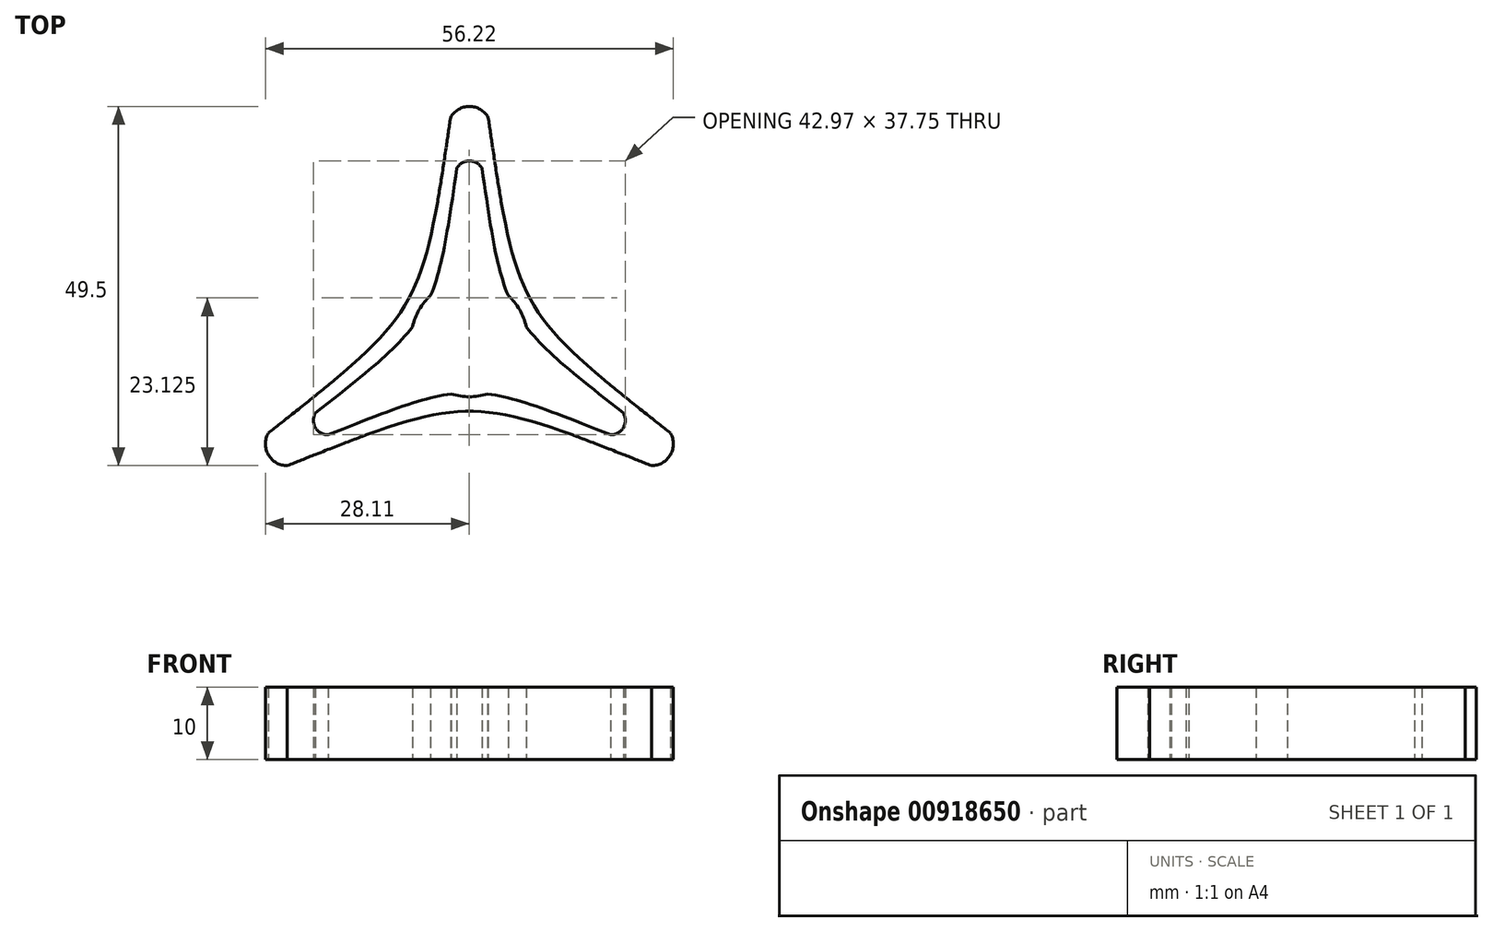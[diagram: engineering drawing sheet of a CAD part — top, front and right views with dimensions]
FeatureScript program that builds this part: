
annotation { "Feature Type Name" : "Feature", "Feature Type Description" : "" }
export const myFeature = defineFeature(function(context is Context, id is Id, definition is map)
    precondition{}
    {
        {
            var Q0;
            Q0=qCreatedBy(makeId("Top.planeOp"),FACE);
            var sketch = newSketch(context, id + "F0", { "sketchPlane" : qUnion([Q0])});
            skCircle(sketch, "E0", {"center": v(0, 0) * mm, "radius": 8 * mm});
            skCircle(sketch, "E1", {"center": v(0, 0) * mm, "radius": 35 * mm});
            skCircle(sketch, "E2", {"center": v(0, 0) * mm, "radius": 26.5 * mm});
            skCircle(sketch, "E3", {"center": v(0, 0) * mm, "radius": 5.5 * mm});
            skCircle(sketch, "E4", {"center": v(0, 0) * mm, "radius": 7.5 * mm});
            skCircle(sketch, "E5.cCircle", {"center": v(0, 0) * mm, "radius": 5.5 * mm, "construction": true});
            skLineSegment(sketch, "E5.0", {"start": v(0, -5.5) * mm, "end": v(-4.76, 2.75) * mm});
            skLineSegment(sketch, "E5.1", {"start": v(-4.76, 2.75) * mm, "end": v(4.76, 2.75) * mm});
            skLineSegment(sketch, "E5.2", {"start": v(4.76, 2.75) * mm, "end": v(0, -5.5) * mm});
            skCircle(sketch, "E6.cCircle", {"center": v(0, 0) * mm, "radius": 7.5 * mm, "construction": true});
            skLineSegment(sketch, "E6.0", {"start": v(0, -7.5) * mm, "end": v(-6.5, 3.75) * mm});
            skLineSegment(sketch, "E6.1", {"start": v(-6.5, 3.75) * mm, "end": v(6.5, 3.75) * mm});
            skLineSegment(sketch, "E6.2", {"start": v(6.5, 3.75) * mm, "end": v(0, -7.5) * mm});
            skCircle(sketch, "E7.cCircle", {"center": v(0, 0) * mm, "radius": 26.5 * mm, "construction": true});
            skPoint(sketch, "E7.cCircle.perimeterSnap0", {"position": v(0, 3.75) * mm});
            skLineSegment(sketch, "E7.0", {"start": v(1.73, 23.5) * mm, "end": v(21.22, -10.25) * mm});
            skPoint(sketch, "E7.0.startSnap0", {"position": v(0, 3.75) * mm});
            skLineSegment(sketch, "E7.1", {"start": v(19.49, -13.25) * mm, "end": v(-19.49, -13.25) * mm});
            skLineSegment(sketch, "E7.2", {"start": v(-21.22, -10.25) * mm, "end": v(-1.73, 23.5) * mm});
            skCircle(sketch, "E8.cCircle", {"center": v(0, 0) * mm, "radius": 35 * mm, "construction": true});
            skLineSegment(sketch, "E8.0", {"start": v(2.6, 30.5) * mm, "end": v(27.71, -13) * mm});
            skLineSegment(sketch, "E8.1", {"start": v(25.11, -17.5) * mm, "end": v(-25.11, -17.5) * mm});
            skLineSegment(sketch, "E8.2", {"start": v(-27.71, -13) * mm, "end": v(-2.6, 30.5) * mm});
            skPoint(sketch, "E9.visualSharp", {"position": v(0, 35) * mm});
            skArc(sketch, "E9.filletArc", {"start": v(2.6, 30.5) * mm, "mid": v(0, 32) * mm, "end": v(-2.6, 30.5) * mm});
            skPoint(sketch, "E10.visualSharp", {"position": v(30.31, -17.5) * mm});
            skArc(sketch, "E10.filletArc", {"start": v(25.11, -17.5) * mm, "mid": v(27.71, -16) * mm, "end": v(27.71, -13) * mm});
            skPoint(sketch, "E11.visualSharp", {"position": v(-30.31, -17.5) * mm});
            skArc(sketch, "E11.filletArc", {"start": v(-27.71, -13) * mm, "mid": v(-27.71, -16) * mm, "end": v(-25.11, -17.5) * mm});
            skPoint(sketch, "E12.visualSharp", {"position": v(0, 26.5) * mm});
            skArc(sketch, "E12.filletArc", {"start": v(1.73, 23.5) * mm, "mid": v(0, 24.5) * mm, "end": v(-1.73, 23.5) * mm});
            skPoint(sketch, "E13.visualSharp", {"position": v(22.95, -13.25) * mm});
            skArc(sketch, "E13.filletArc", {"start": v(19.49, -13.25) * mm, "mid": v(21.22, -12.25) * mm, "end": v(21.22, -10.25) * mm});
            skPoint(sketch, "E14.visualSharp", {"position": v(-22.95, -13.25) * mm});
            skArc(sketch, "E14.filletArc", {"start": v(-21.22, -10.25) * mm, "mid": v(-21.22, -12.25) * mm, "end": v(-19.49, -13.25) * mm});
            skFitSpline(sketch, "E15", {"points": [v(-2.6, 30.5) * mm, v(-27.71, -13) * mm], "startDerivative": vector(-11.7, -80.25) * mm, "endDerivative": vector(-63.65, -50.25) * mm});
            skFitSpline(sketch, "E16", {"points": [v(-1.73, 23.5) * mm, v(-21.22, -10.25) * mm], "startDerivative": vector(-9.1, -62.25) * mm, "endDerivative": vector(-49.36, -39) * mm});
            skFitSpline(sketch, "E17", {"points": [v(-19.49, -13.25) * mm, v(19.49, -13.25) * mm], "startDerivative": vector(58.46, 23.25) * mm, "endDerivative": vector(58.46, -23.25) * mm});
            skFitSpline(sketch, "E18", {"points": [v(-25.11, -17.5) * mm, v(25.11, -17.5) * mm], "startDerivative": vector(75.34, 30) * mm, "endDerivative": vector(75.34, -30) * mm});
            skFitSpline(sketch, "E19", {"points": [v(27.71, -13) * mm, v(2.6, 30.5) * mm], "startDerivative": vector(-63.65, 50.25) * mm, "endDerivative": vector(-11.7, 80.25) * mm});
            skFitSpline(sketch, "E20", {"points": [v(1.73, 23.5) * mm, v(21.22, -10.25) * mm], "startDerivative": vector(9.1, -62.25) * mm, "endDerivative": vector(49.36, -39) * mm});
            skSolve(sketch);
        }
        {
            var Q0;
            {var subQ5=sQuery(id+"F0.wireOp",EDGE,"E9.filletArc");Q0=makeQuery(id+"F0.imprint","IMPRINT",FACE,{"disambiguationData":[TD([[makeQuery(id+"F0.imprint","IMPRINT",EDGE,{"derivedFrom":subQ5}),1.0]])]});}
            var Q1;
            {var subQ0=sQuery(id+"F0.wireOp",EDGE,"E12.filletArc");Q1=makeQuery(id+"F0.imprint","IMPRINT",FACE,{"disambiguationData":[TD([[makeQuery(id+"F0.imprint","IMPRINT",EDGE,{"derivedFrom":subQ0}),-1.0]])]});}
            var Q2;
            {var subQ0=sQuery(id+"F0.wireOp",EDGE,"E20");var subQ7=sQuery(id+"F0.wireOp",EDGE,"E0");var subQ8=makeQuery(id+"F0.imprint","INTERSECT",VERTEX,{"disambiguationData":[OD(0.0)],"derivedFrom":[subQ7,subQ0]});Q2=makeQuery(id+"F0.imprint","IMPRINT",FACE,{"disambiguationData":[TD([[makeQuery(id+"F0.imprint","IMPRINT",EDGE,{"disambiguationData":[TD([[subQ8,1.0]])],"derivedFrom":subQ7}),-1.0]])]});}
            var Q3;
            {var subQ0=sQuery(id+"F0.wireOp",EDGE,"E16");var subQ7=sQuery(id+"F0.wireOp",EDGE,"E0");var subQ8=makeQuery(id+"F0.imprint","INTERSECT",VERTEX,{"disambiguationData":[OD(0.0)],"derivedFrom":[subQ7,subQ0]});Q3=makeQuery(id+"F0.imprint","IMPRINT",FACE,{"disambiguationData":[TD([[makeQuery(id+"F0.imprint","IMPRINT",EDGE,{"disambiguationData":[TD([[subQ8,-1.0]])],"derivedFrom":subQ7}),-1.0]])]});}
            var Q4;
            {var subQ0=sQuery(id+"F0.wireOp",EDGE,"E14.filletArc");Q4=makeQuery(id+"F0.imprint","IMPRINT",FACE,{"disambiguationData":[TD([[makeQuery(id+"F0.imprint","IMPRINT",EDGE,{"derivedFrom":subQ0}),-1.0]])]});}
            var Q5;
            {var subQ5=sQuery(id+"F0.wireOp",EDGE,"E11.filletArc");Q5=makeQuery(id+"F0.imprint","IMPRINT",FACE,{"disambiguationData":[TD([[makeQuery(id+"F0.imprint","IMPRINT",EDGE,{"derivedFrom":subQ5}),1.0]])]});}
            var Q6;
            {var subQ0=sQuery(id+"F0.wireOp",EDGE,"E17");var subQ3=sQuery(id+"F0.wireOp",EDGE,"E0");var subQ4=makeQuery(id+"F0.imprint","INTERSECT",VERTEX,{"disambiguationData":[OD(0.0)],"derivedFrom":[subQ3,subQ0]});Q6=makeQuery(id+"F0.imprint","IMPRINT",FACE,{"disambiguationData":[TD([[makeQuery(id+"F0.imprint","IMPRINT",EDGE,{"disambiguationData":[TD([[subQ4,-1.0]])],"derivedFrom":subQ3}),-1.0]])]});}
            var Q7;
            {var subQ0=sQuery(id+"F0.wireOp",EDGE,"E13.filletArc");Q7=makeQuery(id+"F0.imprint","IMPRINT",FACE,{"disambiguationData":[TD([[makeQuery(id+"F0.imprint","IMPRINT",EDGE,{"derivedFrom":subQ0}),-1.0]])]});}
            var Q8;
            {var subQ5=sQuery(id+"F0.wireOp",EDGE,"E10.filletArc");Q8=makeQuery(id+"F0.imprint","IMPRINT",FACE,{"disambiguationData":[TD([[makeQuery(id+"F0.imprint","IMPRINT",EDGE,{"derivedFrom":subQ5}),1.0]])]});}
            extrude(context, id + "F1", {"entities" : qUnion([Q0, Q1, Q2, Q3, Q4, Q5, Q6, Q7, Q8]), "depth" : 10 * mm, "offsetDistance" : 25 * mm});
        }
        {
            var Q0;
            {var subQ5=sQuery(id+"F0.wireOp",EDGE,"E9.filletArc");Q0=makeQuery(id+"F0.imprint","IMPRINT",FACE,{"disambiguationData":[TD([[makeQuery(id+"F0.imprint","IMPRINT",EDGE,{"derivedFrom":subQ5}),1.0]])]});}
            var Q1;
            {var subQ0=sQuery(id+"F0.wireOp",EDGE,"E12.filletArc");Q1=makeQuery(id+"F0.imprint","IMPRINT",FACE,{"disambiguationData":[TD([[makeQuery(id+"F0.imprint","IMPRINT",EDGE,{"derivedFrom":subQ0}),-1.0]])]});}
            var Q2;
            {var subQ0=sQuery(id+"F0.wireOp",EDGE,"E20");var subQ7=sQuery(id+"F0.wireOp",EDGE,"E0");var subQ8=makeQuery(id+"F0.imprint","INTERSECT",VERTEX,{"disambiguationData":[OD(0.0)],"derivedFrom":[subQ7,subQ0]});Q2=makeQuery(id+"F0.imprint","IMPRINT",FACE,{"disambiguationData":[TD([[makeQuery(id+"F0.imprint","IMPRINT",EDGE,{"disambiguationData":[TD([[subQ8,1.0]])],"derivedFrom":subQ7}),-1.0]])]});}
            var Q3;
            {var subQ0=sQuery(id+"F0.wireOp",EDGE,"E16");var subQ7=sQuery(id+"F0.wireOp",EDGE,"E0");var subQ8=makeQuery(id+"F0.imprint","INTERSECT",VERTEX,{"disambiguationData":[OD(0.0)],"derivedFrom":[subQ7,subQ0]});Q3=makeQuery(id+"F0.imprint","IMPRINT",FACE,{"disambiguationData":[TD([[makeQuery(id+"F0.imprint","IMPRINT",EDGE,{"disambiguationData":[TD([[subQ8,-1.0]])],"derivedFrom":subQ7}),-1.0]])]});}
            var Q4;
            {var subQ0=sQuery(id+"F0.wireOp",EDGE,"E17");var subQ3=sQuery(id+"F0.wireOp",EDGE,"E0");var subQ4=makeQuery(id+"F0.imprint","INTERSECT",VERTEX,{"disambiguationData":[OD(0.0)],"derivedFrom":[subQ3,subQ0]});Q4=makeQuery(id+"F0.imprint","IMPRINT",FACE,{"disambiguationData":[TD([[makeQuery(id+"F0.imprint","IMPRINT",EDGE,{"disambiguationData":[TD([[subQ4,-1.0]])],"derivedFrom":subQ3}),-1.0]])]});}
            var Q5;
            {var subQ0=sQuery(id+"F0.wireOp",EDGE,"E14.filletArc");Q5=makeQuery(id+"F0.imprint","IMPRINT",FACE,{"disambiguationData":[TD([[makeQuery(id+"F0.imprint","IMPRINT",EDGE,{"derivedFrom":subQ0}),-1.0]])]});}
            var Q6;
            {var subQ5=sQuery(id+"F0.wireOp",EDGE,"E11.filletArc");Q6=makeQuery(id+"F0.imprint","IMPRINT",FACE,{"disambiguationData":[TD([[makeQuery(id+"F0.imprint","IMPRINT",EDGE,{"derivedFrom":subQ5}),1.0]])]});}
            var Q7;
            {var subQ0=sQuery(id+"F0.wireOp",EDGE,"E13.filletArc");Q7=makeQuery(id+"F0.imprint","IMPRINT",FACE,{"disambiguationData":[TD([[makeQuery(id+"F0.imprint","IMPRINT",EDGE,{"derivedFrom":subQ0}),-1.0]])]});}
            var Q8;
            {var subQ5=sQuery(id+"F0.wireOp",EDGE,"E10.filletArc");Q8=makeQuery(id+"F0.imprint","IMPRINT",FACE,{"disambiguationData":[TD([[makeQuery(id+"F0.imprint","IMPRINT",EDGE,{"derivedFrom":subQ5}),1.0]])]});}
            extrude(context, id + "F2", {"entities" : qUnion([Q0, Q1, Q2, Q3, Q4, Q5, Q6, Q7, Q8]), "operationType" : NewBodyOperationType.ADD, "depth" : 10 * mm, "offsetDistance" : 25 * mm});
        }
        {
            var Q0;
            {var subQ0=sQuery(id+"F0.wireOp",EDGE,"E12.filletArc");Q0=makeQuery(id+"F0.imprint","IMPRINT",FACE,{"disambiguationData":[TD([[makeQuery(id+"F0.imprint","IMPRINT",EDGE,{"derivedFrom":subQ0}),-1.0]])]});}
            var Q1;
            {var subQ5=sQuery(id+"F0.wireOp",EDGE,"E9.filletArc");Q1=makeQuery(id+"F0.imprint","IMPRINT",FACE,{"disambiguationData":[TD([[makeQuery(id+"F0.imprint","IMPRINT",EDGE,{"derivedFrom":subQ5}),1.0]])]});}
            var Q2;
            {var subQ0=sQuery(id+"F0.wireOp",EDGE,"E16");var subQ7=sQuery(id+"F0.wireOp",EDGE,"E0");var subQ8=makeQuery(id+"F0.imprint","INTERSECT",VERTEX,{"disambiguationData":[OD(0.0)],"derivedFrom":[subQ7,subQ0]});Q2=makeQuery(id+"F0.imprint","IMPRINT",FACE,{"disambiguationData":[TD([[makeQuery(id+"F0.imprint","IMPRINT",EDGE,{"disambiguationData":[TD([[subQ8,-1.0]])],"derivedFrom":subQ7}),-1.0]])]});}
            var Q3;
            {var subQ0=sQuery(id+"F0.wireOp",EDGE,"E20");var subQ7=sQuery(id+"F0.wireOp",EDGE,"E0");var subQ8=makeQuery(id+"F0.imprint","INTERSECT",VERTEX,{"disambiguationData":[OD(0.0)],"derivedFrom":[subQ7,subQ0]});Q3=makeQuery(id+"F0.imprint","IMPRINT",FACE,{"disambiguationData":[TD([[makeQuery(id+"F0.imprint","IMPRINT",EDGE,{"disambiguationData":[TD([[subQ8,1.0]])],"derivedFrom":subQ7}),-1.0]])]});}
            var Q4;
            {var subQ0=sQuery(id+"F0.wireOp",EDGE,"E14.filletArc");Q4=makeQuery(id+"F0.imprint","IMPRINT",FACE,{"disambiguationData":[TD([[makeQuery(id+"F0.imprint","IMPRINT",EDGE,{"derivedFrom":subQ0}),-1.0]])]});}
            var Q5;
            {var subQ5=sQuery(id+"F0.wireOp",EDGE,"E11.filletArc");Q5=makeQuery(id+"F0.imprint","IMPRINT",FACE,{"disambiguationData":[TD([[makeQuery(id+"F0.imprint","IMPRINT",EDGE,{"derivedFrom":subQ5}),1.0]])]});}
            var Q6;
            {var subQ0=sQuery(id+"F0.wireOp",EDGE,"E17");var subQ3=sQuery(id+"F0.wireOp",EDGE,"E0");var subQ4=makeQuery(id+"F0.imprint","INTERSECT",VERTEX,{"disambiguationData":[OD(0.0)],"derivedFrom":[subQ3,subQ0]});Q6=makeQuery(id+"F0.imprint","IMPRINT",FACE,{"disambiguationData":[TD([[makeQuery(id+"F0.imprint","IMPRINT",EDGE,{"disambiguationData":[TD([[subQ4,-1.0]])],"derivedFrom":subQ3}),-1.0]])]});}
            var Q7;
            {var subQ0=sQuery(id+"F0.wireOp",EDGE,"E13.filletArc");Q7=makeQuery(id+"F0.imprint","IMPRINT",FACE,{"disambiguationData":[TD([[makeQuery(id+"F0.imprint","IMPRINT",EDGE,{"derivedFrom":subQ0}),-1.0]])]});}
            var Q8;
            {var subQ5=sQuery(id+"F0.wireOp",EDGE,"E10.filletArc");Q8=makeQuery(id+"F0.imprint","IMPRINT",FACE,{"disambiguationData":[TD([[makeQuery(id+"F0.imprint","IMPRINT",EDGE,{"derivedFrom":subQ5}),1.0]])]});}
            extrude(context, id + "F3", {"entities" : qUnion([Q0, Q1, Q2, Q3, Q4, Q5, Q6, Q7, Q8]), "operationType" : NewBodyOperationType.ADD, "depth" : 6 * mm, "offsetDistance" : 25 * mm});
        }
        {
            var Q0;
            {var subQ5=sQuery(id+"F0.wireOp",EDGE,"E9.filletArc");Q0=makeQuery(id+"F0.imprint","IMPRINT",FACE,{"disambiguationData":[TD([[makeQuery(id+"F0.imprint","IMPRINT",EDGE,{"derivedFrom":subQ5}),1.0]])]});}
            var Q1;
            {var subQ0=sQuery(id+"F0.wireOp",EDGE,"E12.filletArc");Q1=makeQuery(id+"F0.imprint","IMPRINT",FACE,{"disambiguationData":[TD([[makeQuery(id+"F0.imprint","IMPRINT",EDGE,{"derivedFrom":subQ0}),-1.0]])]});}
            var Q2;
            {var subQ0=sQuery(id+"F0.wireOp",EDGE,"E16");var subQ7=sQuery(id+"F0.wireOp",EDGE,"E0");var subQ8=makeQuery(id+"F0.imprint","INTERSECT",VERTEX,{"disambiguationData":[OD(0.0)],"derivedFrom":[subQ7,subQ0]});Q2=makeQuery(id+"F0.imprint","IMPRINT",FACE,{"disambiguationData":[TD([[makeQuery(id+"F0.imprint","IMPRINT",EDGE,{"disambiguationData":[TD([[subQ8,-1.0]])],"derivedFrom":subQ7}),-1.0]])]});}
            var Q3;
            {var subQ0=sQuery(id+"F0.wireOp",EDGE,"E20");var subQ7=sQuery(id+"F0.wireOp",EDGE,"E0");var subQ8=makeQuery(id+"F0.imprint","INTERSECT",VERTEX,{"disambiguationData":[OD(0.0)],"derivedFrom":[subQ7,subQ0]});Q3=makeQuery(id+"F0.imprint","IMPRINT",FACE,{"disambiguationData":[TD([[makeQuery(id+"F0.imprint","IMPRINT",EDGE,{"disambiguationData":[TD([[subQ8,1.0]])],"derivedFrom":subQ7}),-1.0]])]});}
            var Q4;
            {var subQ0=sQuery(id+"F0.wireOp",EDGE,"E17");var subQ3=sQuery(id+"F0.wireOp",EDGE,"E0");var subQ4=makeQuery(id+"F0.imprint","INTERSECT",VERTEX,{"disambiguationData":[OD(0.0)],"derivedFrom":[subQ3,subQ0]});Q4=makeQuery(id+"F0.imprint","IMPRINT",FACE,{"disambiguationData":[TD([[makeQuery(id+"F0.imprint","IMPRINT",EDGE,{"disambiguationData":[TD([[subQ4,-1.0]])],"derivedFrom":subQ3}),-1.0]])]});}
            var Q5;
            {var subQ5=sQuery(id+"F0.wireOp",EDGE,"E10.filletArc");Q5=makeQuery(id+"F0.imprint","IMPRINT",FACE,{"disambiguationData":[TD([[makeQuery(id+"F0.imprint","IMPRINT",EDGE,{"derivedFrom":subQ5}),1.0]])]});}
            var Q6;
            {var subQ0=sQuery(id+"F0.wireOp",EDGE,"E13.filletArc");Q6=makeQuery(id+"F0.imprint","IMPRINT",FACE,{"disambiguationData":[TD([[makeQuery(id+"F0.imprint","IMPRINT",EDGE,{"derivedFrom":subQ0}),-1.0]])]});}
            var Q7;
            {var subQ0=sQuery(id+"F0.wireOp",EDGE,"E14.filletArc");Q7=makeQuery(id+"F0.imprint","IMPRINT",FACE,{"disambiguationData":[TD([[makeQuery(id+"F0.imprint","IMPRINT",EDGE,{"derivedFrom":subQ0}),-1.0]])]});}
            var Q8;
            {var subQ5=sQuery(id+"F0.wireOp",EDGE,"E11.filletArc");Q8=makeQuery(id+"F0.imprint","IMPRINT",FACE,{"disambiguationData":[TD([[makeQuery(id+"F0.imprint","IMPRINT",EDGE,{"derivedFrom":subQ5}),1.0]])]});}
            extrude(context, id + "F4", {"entities" : qUnion([Q0, Q1, Q2, Q3, Q4, Q5, Q6, Q7, Q8]), "operationType" : NewBodyOperationType.ADD, "depth" : 6 * mm, "offsetDistance" : 25 * mm});
        }
        {
            var Q0;
            {var subQ5=sQuery(id+"F0.wireOp",EDGE,"E9.filletArc");Q0=makeQuery(id+"F0.imprint","IMPRINT",FACE,{"disambiguationData":[TD([[makeQuery(id+"F0.imprint","IMPRINT",EDGE,{"derivedFrom":subQ5}),1.0]])]});}
            var Q1;
            {var subQ0=sQuery(id+"F0.wireOp",EDGE,"E12.filletArc");Q1=makeQuery(id+"F0.imprint","IMPRINT",FACE,{"disambiguationData":[TD([[makeQuery(id+"F0.imprint","IMPRINT",EDGE,{"derivedFrom":subQ0}),-1.0]])]});}
            var Q2;
            {var subQ0=sQuery(id+"F0.wireOp",EDGE,"E16");var subQ7=sQuery(id+"F0.wireOp",EDGE,"E0");var subQ8=makeQuery(id+"F0.imprint","INTERSECT",VERTEX,{"disambiguationData":[OD(0.0)],"derivedFrom":[subQ7,subQ0]});Q2=makeQuery(id+"F0.imprint","IMPRINT",FACE,{"disambiguationData":[TD([[makeQuery(id+"F0.imprint","IMPRINT",EDGE,{"disambiguationData":[TD([[subQ8,-1.0]])],"derivedFrom":subQ7}),-1.0]])]});}
            var Q3;
            {var subQ0=sQuery(id+"F0.wireOp",EDGE,"E20");var subQ7=sQuery(id+"F0.wireOp",EDGE,"E0");var subQ8=makeQuery(id+"F0.imprint","INTERSECT",VERTEX,{"disambiguationData":[OD(0.0)],"derivedFrom":[subQ7,subQ0]});Q3=makeQuery(id+"F0.imprint","IMPRINT",FACE,{"disambiguationData":[TD([[makeQuery(id+"F0.imprint","IMPRINT",EDGE,{"disambiguationData":[TD([[subQ8,1.0]])],"derivedFrom":subQ7}),-1.0]])]});}
            var Q4;
            {var subQ0=sQuery(id+"F0.wireOp",EDGE,"E17");var subQ3=sQuery(id+"F0.wireOp",EDGE,"E0");var subQ4=makeQuery(id+"F0.imprint","INTERSECT",VERTEX,{"disambiguationData":[OD(0.0)],"derivedFrom":[subQ3,subQ0]});Q4=makeQuery(id+"F0.imprint","IMPRINT",FACE,{"disambiguationData":[TD([[makeQuery(id+"F0.imprint","IMPRINT",EDGE,{"disambiguationData":[TD([[subQ4,-1.0]])],"derivedFrom":subQ3}),-1.0]])]});}
            var Q5;
            {var subQ0=sQuery(id+"F0.wireOp",EDGE,"E14.filletArc");Q5=makeQuery(id+"F0.imprint","IMPRINT",FACE,{"disambiguationData":[TD([[makeQuery(id+"F0.imprint","IMPRINT",EDGE,{"derivedFrom":subQ0}),-1.0]])]});}
            var Q6;
            {var subQ0=sQuery(id+"F0.wireOp",EDGE,"E13.filletArc");Q6=makeQuery(id+"F0.imprint","IMPRINT",FACE,{"disambiguationData":[TD([[makeQuery(id+"F0.imprint","IMPRINT",EDGE,{"derivedFrom":subQ0}),-1.0]])]});}
            var Q7;
            {var subQ5=sQuery(id+"F0.wireOp",EDGE,"E10.filletArc");Q7=makeQuery(id+"F0.imprint","IMPRINT",FACE,{"disambiguationData":[TD([[makeQuery(id+"F0.imprint","IMPRINT",EDGE,{"derivedFrom":subQ5}),1.0]])]});}
            var Q8;
            {var subQ5=sQuery(id+"F0.wireOp",EDGE,"E11.filletArc");Q8=makeQuery(id+"F0.imprint","IMPRINT",FACE,{"disambiguationData":[TD([[makeQuery(id+"F0.imprint","IMPRINT",EDGE,{"derivedFrom":subQ5}),1.0]])]});}
            extrude(context, id + "F5", {"entities" : qUnion([Q0, Q1, Q2, Q3, Q4, Q5, Q6, Q7, Q8]), "operationType" : NewBodyOperationType.ADD, "depth" : 6 * mm, "offsetDistance" : 25 * mm});
        }
    });
